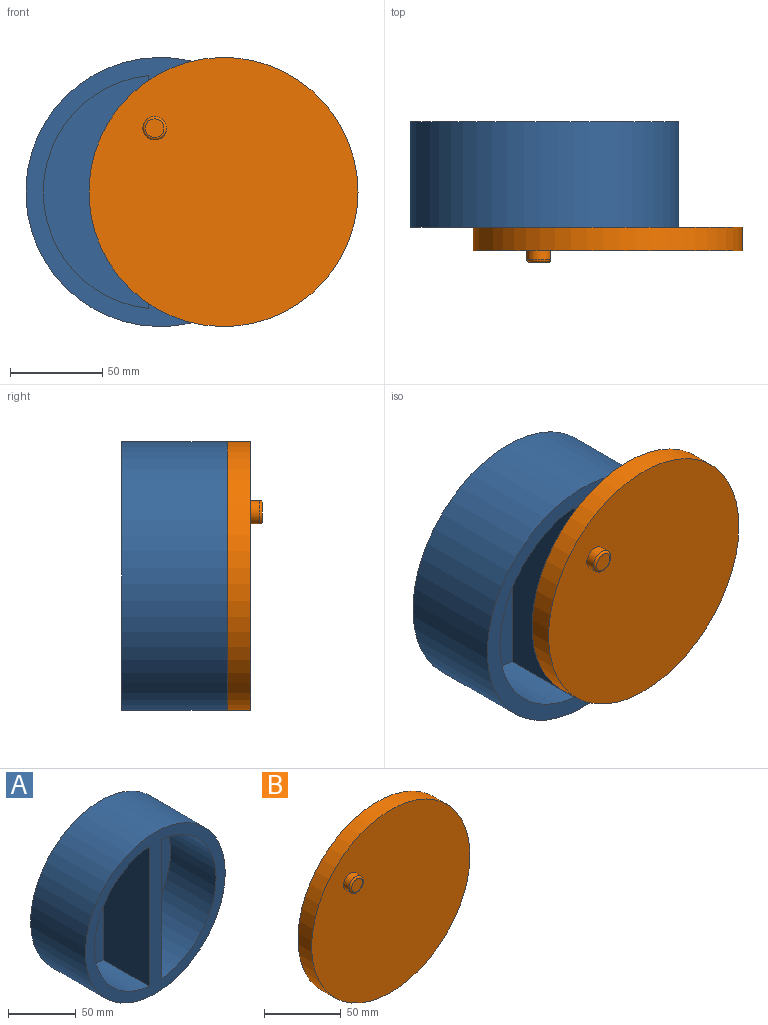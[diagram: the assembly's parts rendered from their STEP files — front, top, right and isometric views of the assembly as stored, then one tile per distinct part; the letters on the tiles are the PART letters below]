
ASSEMBLY  parts=2 mates=1
PART A: 9 faces, bbox 146.1x57.2x146.1 mm
  f0: cylinder r=63.5mm len=126.36mm, axis (0,-1,0), area 8894.9mm2, adj f1,f4,f7
  f1: plane 126.36x57.15mm, normal (0,-1,0), area 5528.7mm2, adj f0,f7
  f2: cylinder r=73.03mm len=146.05mm, axis (0,-1,0), area 26222.1mm2, adj f3,f4
  f3: plane 146.05x146.05mm, normal (0,1,0), area 16753mm2, adj f2
  f4: plane 146.05x146.05mm, normal (0,-1,0), area 5695.5mm2, adj f0,f2,f5,f7,f8
  f5: cylinder r=63.5mm len=126.36mm, axis (0,-1,0), area 8894.9mm2, adj f4,f6,f8
  f6: plane 126.36x57.15mm, normal (0,-1,0), area 5528.7mm2, adj f5,f8
  f7: plane 126.36x47.63mm, normal (1,0,0), area 6018.1mm2, adj f0,f1,f4
  f8: plane 126.36x47.63mm, normal (-1,0,0), area 6018.1mm2, adj f4,f5,f6
PART B: 6 faces, bbox 146.1x19.1x146.1 mm
  f0: cylinder r=73.03mm len=146.05mm, axis (0,1,0), area 5827.1mm2, adj f1,f2
  f1: plane 146.05x146.05mm, normal (0,-1,0), area 16626.3mm2, adj f0,f3
  f2: plane 146.05x146.05mm, normal (0,1,0), area 16753mm2, adj f0
  f3: cylinder r=6.35mm len=12.7mm, axis (0,1,0), area 202.7mm2, adj f1,f5
  f4: plane 10.16x10.16mm, normal (0,-1,0), area 81.1mm2, adj f5
  f5: torus R=5.08mm, axis (0,-1,0), area 73.8mm2, adj f3,f4
PLACE A t=(-44.39,-22.79,-23.7)mm
PLACE B t=(-10.1,34.36,-23.7)mm
MATE planar B.f0 <-> A.f0  axis (0,1,0) through (-10.1,-22.79,-23.7)mm
